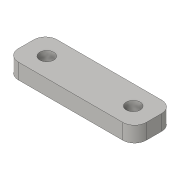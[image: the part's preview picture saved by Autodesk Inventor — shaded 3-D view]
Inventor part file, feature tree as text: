
AUTODESK INVENTOR PART (.ipt)
format: ipt  version: 2016 (Build 200138000, 138)  size: 94,208 bytes
history: native  units: in
note: dims shown in document units (in); Inventor stores cm internally (conversion verified against a paired STEP export)
features: extrude x2, sketch x2, plane x1, mirror x1, fillet x1
ambient origin geometry x8: Origin, YZ Plane, XZ Plane, XY Plane, X Axis, Y Axis, Z Axis, Center Point
bodies: Solid1 (feature_tree)
feature tree (7):
  extrude  "Extrusion1"  Depth=0.3937in
  extrude  "Extrusion2"  Depth=0.1575in TaperAngle=0.0deg
  plane  "Work Plane1"
  mirror  "Mirror1"
  fillet  "Fillet1"  [1 undecoded]
  sketch  "Sketch1"  dims[d0=1.2992in d1=0.3937in]
  sketch  "Sketch2"  dims[d2=0.1575in d3=0.0in d5=0.1575in d6=0.0in d7=-0.6496in d8=0.1181in d9=0.1417in]
note: 1 required parameter value undecoded (feature->parameter linkage not recoverable at this tier; creation-order binding heuristic only, values carry confidence <= 0.55)
